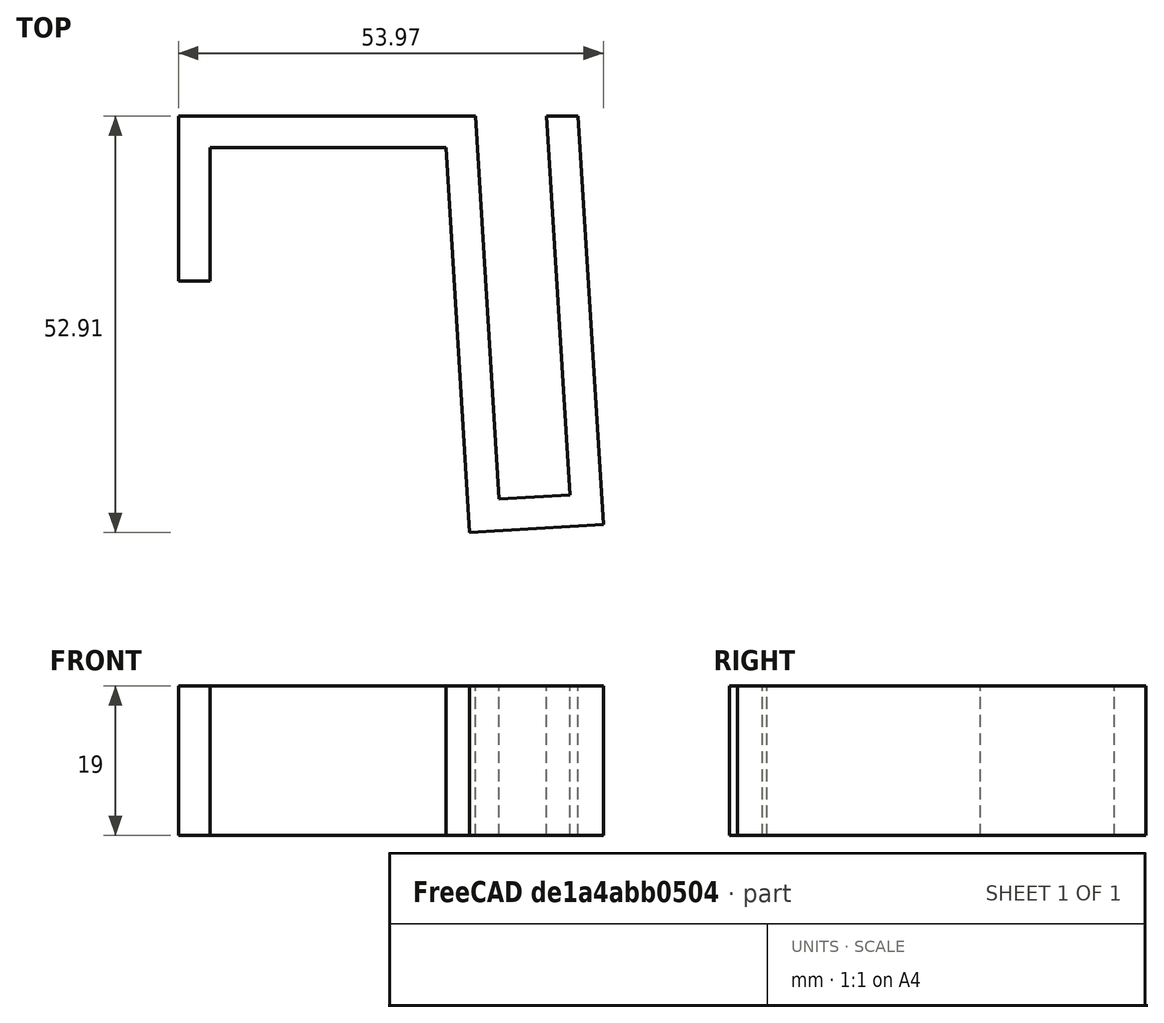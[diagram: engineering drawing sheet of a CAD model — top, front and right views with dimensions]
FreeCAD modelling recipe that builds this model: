
FCSTD DOCUMENT  (FreeCAD 0.18R16146 (Git))
Label: laundry sink hangers2
License: All rights reserved
LicenseURL: http://en.wikipedia.org/wiki/All_rights_reserved
objects: Sketcher::SketchObject×1, PartDesign::Pad×1, PartDesign::Body×1
note: 4 computed .brp shape members not serialized (recipe doc carries the construction recipe); baked Part::Feature solids carry a one-line shape summary decoded from their .brp

FEATURE [Sketcher::SketchObject] Sketch
  MapMode = 5
  Support = -> [XY_Plane]
  sketch-geometry (13):
    g0: LineSegment StartX=0 StartY=0 StartZ=0 EndX=0 EndY=17 EndZ=0
    g1: LineSegment StartX=0 StartY=17 StartZ=0 EndX=30 EndY=17 EndZ=0
    g2: LineSegment StartX=30 StartY=17 StartZ=0 EndX=33 EndY=-31.9081 EndZ=0
    g3: LineSegment StartX=33 StartY=-31.9081 StartZ=0 EndX=49.9681 EndY=-30.8673 EndZ=0
    g4: LineSegment StartX=49.9681 StartY=-30.8673 StartZ=0 EndX=46.7866 EndY=21 EndZ=0
    g5: LineSegment StartX=46.7866 StartY=21 StartZ=0 EndX=42.7791 EndY=21 EndZ=0
    g6: LineSegment StartX=42.7791 StartY=21 StartZ=0 EndX=45.7307 EndY=-27.1197 EndZ=0
    g7: LineSegment StartX=36.7476 StartY=-27.6707 StartZ=0 EndX=33.7622 EndY=21 EndZ=0
    g8: LineSegment StartX=33.7622 StartY=21 StartZ=0 EndX=-4 EndY=21 EndZ=0
    g9: LineSegment StartX=-4 StartY=21 StartZ=0 EndX=-4 EndY=0 EndZ=0
    g10: LineSegment StartX=-4 StartY=0 StartZ=0 EndX=0 EndY=0 EndZ=0
    g11: LineSegment StartX=36.7476 StartY=-27.6707 StartZ=0 EndX=45.7307 EndY=-27.1197 EndZ=0
    g12: LineSegment [constr] StartX=33.7622 StartY=21 StartZ=0 EndX=42.7791 EndY=21 EndZ=0
  constraints (37):
    c: Coincident(g-1,g0)
    c: Vertical(g0)
    c: Coincident(g0,g1)
    c: Horizontal(g1)
    c: Coincident(g1,g2)
    c: Coincident(g2,g3)
    c: Coincident(g3,g4)
    c: Coincident(g4,g5)
    c: Coincident(g5,g6)
    c: Coincident(g7,g8)
    c: Horizontal(g8)
    c: Coincident(g8,g9)
    c: PointOnObject(g9,g-1)
    c: Vertical(g9)
    c: Coincident(g9,g10)
    c: Coincident(g10,g0)
    c: Distance(g0) = 17
    c: Distance(g1) = 30
    c: Distance(g2) = 49
    c: Parallel(g2,g7)
    c: Parallel(g6,g4)
    c: Horizontal(g5)
    c: DistanceX(g0,g2) = 33
    c: DistanceX(g8,g0) = 4
    c: DistanceY(g0,g8) = 4
    c: Coincident(g11,g6)
    c: Distance(g11) = 9
    c: Parallel(g11,g3)
    c: Coincident(g12,g7)
    c: Coincident(g12,g5)
    c: Horizontal(g12)
    c: Coincident(g11,g7)
    c: Parallel(g6,g7)
    c: Distance(g7,g2) = 4
    c: Distance(g6,g4) = 4
    c: Distance(g6,g3) = 4
    c: Angle(g11,g7) = 1.5708
FEATURE [PartDesign::Pad] Pad
  Length = 19
  Length2 = 100
  Profile = -> Sketch
  Type = 0
FEATURE [PartDesign::Body] Body
  Group = -> [Sketch,Pad]
  Origin = -> Origin
  Tip = -> Pad
